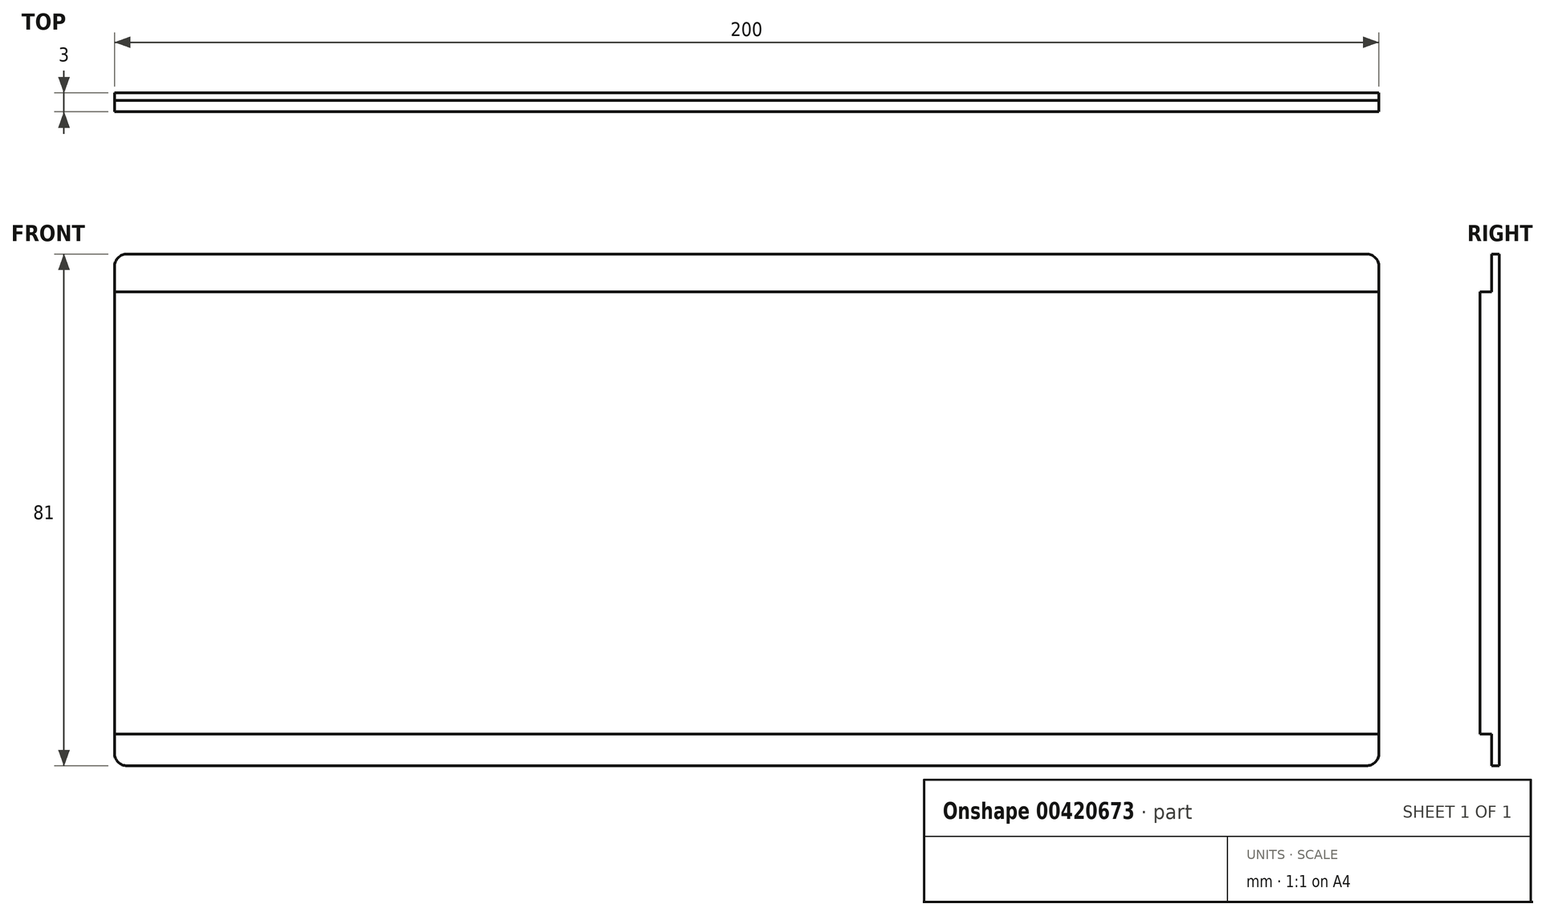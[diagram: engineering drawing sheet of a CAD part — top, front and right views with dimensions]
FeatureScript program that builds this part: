
annotation { "Feature Type Name" : "Feature", "Feature Type Description" : "" }
export const myFeature = defineFeature(function(context is Context, id is Id, definition is map)
    precondition{}
    {
        {
            var Q0;
            Q0=qCreatedBy(makeId("Front.planeOp"),FACE);
            var sketch = newSketch(context, id + "F0", { "sketchPlane" : qUnion([Q0])});
            skLineSegment(sketch, "E0.bottom", {"start": v(100, -40.5) * mm, "end": v(-100, -40.5) * mm});
            skLineSegment(sketch, "E0.top", {"start": v(100, 40.5) * mm, "end": v(-100, 40.5) * mm});
            skLineSegment(sketch, "E0.left", {"start": v(100, -40.5) * mm, "end": v(100, 40.5) * mm});
            skLineSegment(sketch, "E0.right", {"start": v(-100, -40.5) * mm, "end": v(-100, 40.5) * mm});
            skPoint(sketch, "E0.middle", {"position": v(0, 0) * mm});
            skSolve(sketch);
        }
        {
            var Q0;
            Q0=qSketchRegion(id+"F0",true);
            extrude(context, id + "F1", {"entities" : qUnion([Q0]), "depth" : 3 * mm});
        }
        {
            var Q0;
            Q0=makeQuery(id+"F1.opExtrude","CAP_FACE",FACE,{"disambiguationData":[OSD([sQuery(id+"F0.wireOp",EDGE,"E0.bottom"),sQuery(id+"F0.wireOp",EDGE,"E0.top"),sQuery(id+"F0.wireOp",EDGE,"E0.left"),sQuery(id+"F0.wireOp",EDGE,"E0.right")])],"isStart":false});
            var sketch = newSketch(context, id + "F2", { "sketchPlane" : qUnion([Q0])});
            skLineSegment(sketch, "E1", {"start": v(-100, 40.5) * mm, "end": v(100, 40.5) * mm});
            skLineSegment(sketch, "E2", {"start": v(100, 40.5) * mm, "end": v(100, 34.5) * mm});
            skLineSegment(sketch, "E3", {"start": v(100, 34.5) * mm, "end": v(-100, 34.5) * mm});
            skLineSegment(sketch, "E4", {"start": v(-100, 34.5) * mm, "end": v(-100, 40.5) * mm});
            skLineSegment(sketch, "E5", {"start": v(-100, -40.5) * mm, "end": v(100, -40.5) * mm});
            skLineSegment(sketch, "E6", {"start": v(100, -40.5) * mm, "end": v(100, -35.5) * mm});
            skLineSegment(sketch, "E7", {"start": v(100, -35.5) * mm, "end": v(-100, -35.5) * mm});
            skLineSegment(sketch, "E8", {"start": v(-100, -35.5) * mm, "end": v(-100, -40.5) * mm});
            skSolve(sketch);
        }
        {
            var Q0;
            Q0=qSketchRegion(id+"F2",true);
            extrude(context, id + "F3", {"entities" : qUnion([Q0]), "operationType" : NewBodyOperationType.REMOVE, "oppositeDirection" : true, "depth" : 1.8 * mm});
        }
        {
            var Q0;
            Q0=makeQuery(id+"F1.opExtrude","SWEPT_EDGE",EDGE,{"disambiguationData":[OSD([sQuery(id+"F0.wireOp",EDGE,"E0.bottom"),sQuery(id+"F0.wireOp",EDGE,"E0.right")])]});
            var Q1;
            Q1=makeQuery(id+"F1.opExtrude","SWEPT_EDGE",EDGE,{"disambiguationData":[OSD([sQuery(id+"F0.wireOp",EDGE,"E0.top"),sQuery(id+"F0.wireOp",EDGE,"E0.right")])]});
            var Q2;
            Q2=makeQuery(id+"F1.opExtrude","SWEPT_EDGE",EDGE,{"disambiguationData":[OSD([sQuery(id+"F0.wireOp",EDGE,"E0.bottom"),sQuery(id+"F0.wireOp",EDGE,"E0.left")])]});
            var Q3;
            Q3=makeQuery(id+"F1.opExtrude","SWEPT_EDGE",EDGE,{"disambiguationData":[OSD([sQuery(id+"F0.wireOp",EDGE,"E0.top"),sQuery(id+"F0.wireOp",EDGE,"E0.left")])]});
            fillet(context, id + "F4", {"entities" : qUnion([Q0, Q1, Q2, Q3]), "radius" : 2 * mm, "tangentPropagation" : true, "allowEdgeOverflow" : false});
        }
    });
